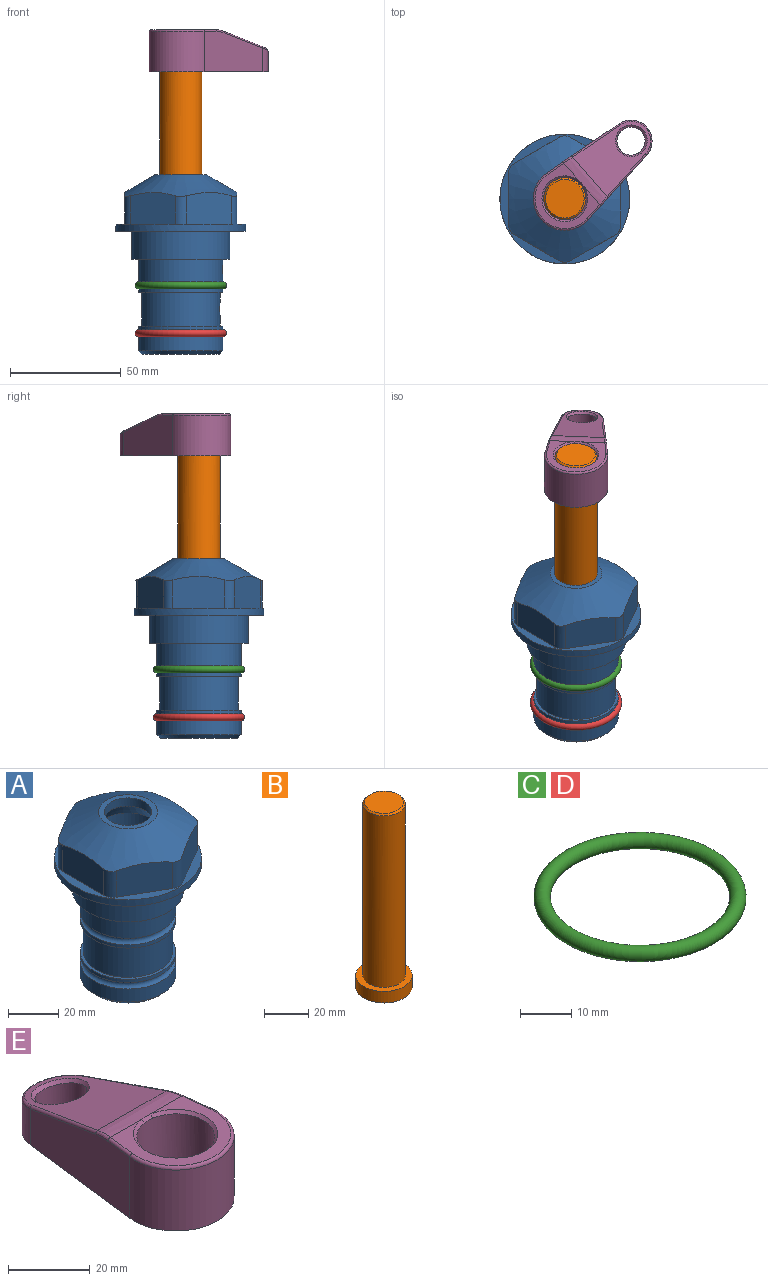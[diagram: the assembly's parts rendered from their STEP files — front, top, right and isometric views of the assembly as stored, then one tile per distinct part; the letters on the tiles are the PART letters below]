
ASSEMBLY  parts=5 mates=4
PART A: 36 faces, bbox 58.7x58.7x81 mm
  f0: cylinder r=17.78mm len=35.56mm, axis (0,0,1), area 1670.8mm2, adj f23,f24,f31
  f1: cylinder r=19.05mm len=38.1mm, axis (0,0,1), area 1191.9mm2, adj f26,f27,f30
  f2: plane 58.66x58.66mm, normal (0,0,-1), area 1150.6mm2, adj f3,f28
  f3: cylinder r=29.33mm len=58.66mm, axis (0,0,-1), area 585.1mm2, adj f2,f4
  f4: plane 58.66x58.66mm, normal (0,0,1), area 475.9mm2, adj f3,f5,f6,f7,f8,f9,f10,f11
  f5: plane 20.32x14.34mm, normal (-0.5,0.87,0), area 324.4mm2, adj f4,f15,f16,f17
  f6: plane 20.32x14.34mm, normal (0.5,0.87,0), area 324.4mm2, adj f4,f14,f15,f17
  f7: plane 23.48x14.34mm, normal (1,0,0), area 324.4mm2, adj f4,f13,f14,f17
  f8: plane 20.32x14.34mm, normal (0.5,-0.87,0), area 324.4mm2, adj f4,f12,f13,f17
  f9: plane 20.32x14.34mm, normal (-0.5,-0.87,0), area 324.4mm2, adj f4,f11,f12,f17
  f10: plane 23.48x14.34mm, normal (-1,0,0), area 324.4mm2, adj f4,f11,f16,f17
  f11: cylinder r=5.08mm len=12.85mm, axis (0,0,-1), area 67.2mm2, adj f4,f9,f10,f17
  f12: cylinder r=5.08mm len=12.85mm, axis (0,0,-1), area 67.2mm2, adj f4,f8,f9,f17
  f13: cylinder r=5.08mm len=12.85mm, axis (0,0,-1), area 67.2mm2, adj f4,f7,f8,f17
  f14: cylinder r=5.08mm len=12.85mm, axis (0,0,-1), area 67.2mm2, adj f4,f6,f7,f17
  f15: cylinder r=5.08mm len=12.85mm, axis (0,0,-1), area 67.2mm2, adj f4,f5,f6,f17
  f16: cylinder r=5.08mm len=12.85mm, axis (0,0,-1), area 67.2mm2, adj f4,f5,f10,f17
  f17: cone r=11.73mm half-angle=60deg, axis (0,0,-1), area 2071.8mm2, adj f5,f6,f7,f8,f9,f10,f11,f12
  f18: plane 23.46x23.46mm, normal (0,0,1), area 147.4mm2, adj f17,f35
  f19: plane 34.93x34.93mm, normal (0,0,-1), area 958mm2, adj f29
  f20: cylinder r=19.05mm len=38.1mm, axis (0,0,1), area 760.1mm2, adj f21,f29
  f21: torus R=19.05mm, axis (0,0,1), area 565.3mm2, adj f20,f22
  f22: cylinder r=19.05mm len=38.1mm, axis (0,0,1), area 190mm2, adj f21,f23
  f23: plane 38.1x38.1mm, normal (0,0,1), area 146.9mm2, adj f0,f22
  f24: plane 38.1x38.1mm, normal (0,0,-1), area 146.9mm2, adj f0,f25
  f25: cylinder r=19.05mm len=38.1mm, axis (0,0,1), area 190mm2, adj f24,f26
  f26: torus R=19.05mm, axis (0,0,1), area 565.3mm2, adj f1,f25
  f27: plane 44.45x44.45mm, normal (0,0,-1), area 411.7mm2, adj f1,f28
  f28: cylinder r=22.23mm len=44.45mm, axis (0,0,1), area 1773.5mm2, adj f2,f27
  f29: cone r=19.05mm half-angle=45deg, axis (0,0,1), area 257.5mm2, adj f19,f20
  f30: cylinder r=3.17mm len=6.75mm, axis (-1,0,0), area 128mm2, adj f1,f33
  f31: cylinder r=3.17mm len=6.35mm, axis (-1,0,0), area 102.5mm2, adj f0,f33
  f32: plane 25.4x25.4mm, normal (0,0,1), area 506.7mm2, adj f33
  f33: cylinder r=12.7mm len=66.42mm, axis (0,0,-1), area 5236.2mm2, adj f30,f31,f32,f34
  f34: cone r=9.53mm half-angle=30deg, axis (0,0,-1), area 443.4mm2, adj f33,f35
  f35: cylinder r=9.53mm len=19.05mm, axis (0,0,-1), area 240.9mm2, adj f18,f34
PART B: 6 faces, bbox 25.4x25.4x101.6 mm
  f0: plane 17.46x17.46mm, normal (0,0,1), area 239.5mm2, adj f5
  f1: plane 25.4x25.4mm, normal (0,0,-1), area 506.7mm2, adj f2
  f2: cylinder r=12.7mm len=25.4mm, axis (0,0,1), area 506.7mm2, adj f1,f3
  f3: plane 25.4x25.4mm, normal (0,0,1), area 221.7mm2, adj f2,f4
  f4: cylinder r=9.53mm len=94.46mm, axis (0,0,1), area 5653mm2, adj f3,f5
  f5: cone r=8.73mm half-angle=45deg, axis (0,0,-1), area 64.4mm2, adj f0,f4
PART C: 1 faces, bbox 44.7x44.7x3.2 mm
  f0: torus R=19.05mm, axis (0,0,1), area 1193.9mm2
PART D: same geometry as C
PART E: 31 faces, bbox 31.7x65.5x19.8 mm
  f0: plane 39.12x18.26mm, normal (0.99,0.12,0), area 612.2mm2, adj f1,f4,f7,f11,f13,f15
  f1: cylinder r=9.53mm len=18.91mm, axis (0,0,-1), area 296.1mm2, adj f0,f2,f7,f17
  f2: plane 39.12x18.26mm, normal (-0.99,0.12,0), area 612.2mm2, adj f1,f4,f7,f12,f14,f16
  f3: cylinder r=6.35mm len=12.7mm, axis (0,0,-1), area 362.4mm2, adj f7,f18
  f4: cylinder r=14.29mm len=28.58mm, axis (0,0,-1), area 882.2mm2, adj f0,f2,f7,f10
  f5: cylinder r=9.53mm len=19.05mm, axis (0,0,-1), area 1092.6mm2, adj f7,f19,f20
  f6: plane 26.99x23.69mm, normal (0,0,1), area 216.2mm2, adj f9,f10,f11,f12,f19
  f7: plane 63.5x28.58mm, normal (0,0,-1), area 661.8mm2, adj f0,f1,f2,f3,f4,f5,f22,f23
  f8: plane 33.52x23.6mm, normal (0,0.26,0.97), area 486mm2, adj f9,f15,f16,f17,f18
  f9: cylinder r=19.05mm len=24.72mm, axis (1,0,0), area 120.4mm2, adj f6,f8,f13,f14,f20
  f10: torus R=13.49mm, axis (0,0,1), area 59mm2, adj f4,f6,f11,f12
  f11: cylinder r=0.79mm len=8.67mm, axis (0.12,-0.99,0), area 10.8mm2, adj f0,f6,f10,f13
  f12: cylinder r=0.79mm len=8.67mm, axis (0.12,0.99,0), area 10.8mm2, adj f2,f6,f10,f14
  f13: bspline ~4.95x1.42mm, area 6.1mm2, adj f0,f9,f11,f15
  f14: bspline ~4.95x1.42mm, area 6.1mm2, adj f2,f9,f12,f16
  f15: cylinder r=0.79mm len=25.95mm, axis (0.12,-0.96,0.26), area 32.9mm2, adj f0,f8,f13,f17
  f16: cylinder r=0.79mm len=25.95mm, axis (0.12,0.96,-0.26), area 32.9mm2, adj f2,f8,f14,f17
  f17: bspline ~18.91x8.38mm, area 30mm2, adj f1,f8,f15,f16
  f18: bspline ~14.29x14.29mm, area 48.3mm2, adj f3,f8
  f19: cone r=9.53mm half-angle=45deg, axis (0,0,1), area 66.5mm2, adj f5,f6,f20
  f20: bspline ~3.22x0.96mm, area 3.5mm2, adj f5,f9,f19
  f21: plane 2.75x2.72mm, normal (0,0,-1), area 2.9mm2, adj f23,f25,f28
  f22: plane 23.05x15.88mm, normal (-0.99,-0.12,0), area 323.6mm2, adj f7,f25,f26,f27,f28,f29
  f23: plane 23.05x15.88mm, normal (0.99,-0.12,0), area 323.6mm2, adj f7,f21,f25,f27,f28,f30
  f24: cylinder r=9.53mm len=10.69mm, axis (0,0,-1), area 114.7mm2, adj f7,f27,f29,f30
  f25: cylinder r=12.7mm len=20.59mm, axis (0,0,-1), area 381.1mm2, adj f7,f21,f22,f23,f26,f28
  f26: plane 2.75x2.72mm, normal (0,0,-1), area 2.9mm2, adj f22,f25,f28
  f27: plane 19.72x18.37mm, normal (0,-0.26,-0.97), area 291.8mm2, adj f22,f23,f24,f28,f29,f30
  f28: cylinder r=15.88mm len=19.92mm, axis (1,0,0), area 54.8mm2, adj f21,f22,f23,f25,f26,f27
  f29: cylinder r=1.59mm len=11mm, axis (0,0,-1), area 34.7mm2, adj f7,f22,f24,f27
  f30: cylinder r=1.59mm len=11mm, axis (0,0,-1), area 34.7mm2, adj f7,f23,f24,f27
PLACE A at identity fixed
PLACE B rot(axis=(0,0,-1),48.9deg) t=(0,0,27.55)mm
PLACE C at identity
PLACE D t=(0,0,-21.59)mm
PLACE E rot(axis=(0,0,-1),48.9deg) t=(0,0,27.55)mm
MATE cylindrical A.f0 <-> B.f2  axis (0,0,1) through (0,0,-50.55)mm
MATE fastened D.f0 <-> A.f0  axis (0,0,1) through (0,0,-46.1)mm
MATE fastened C.f0 <-> A.f0  axis (0,0,1) through (0,0,-24.51)mm
MATE fastened B.f2 <-> E.f4  axis (0,0,1) through (0,0,91.05)mm
